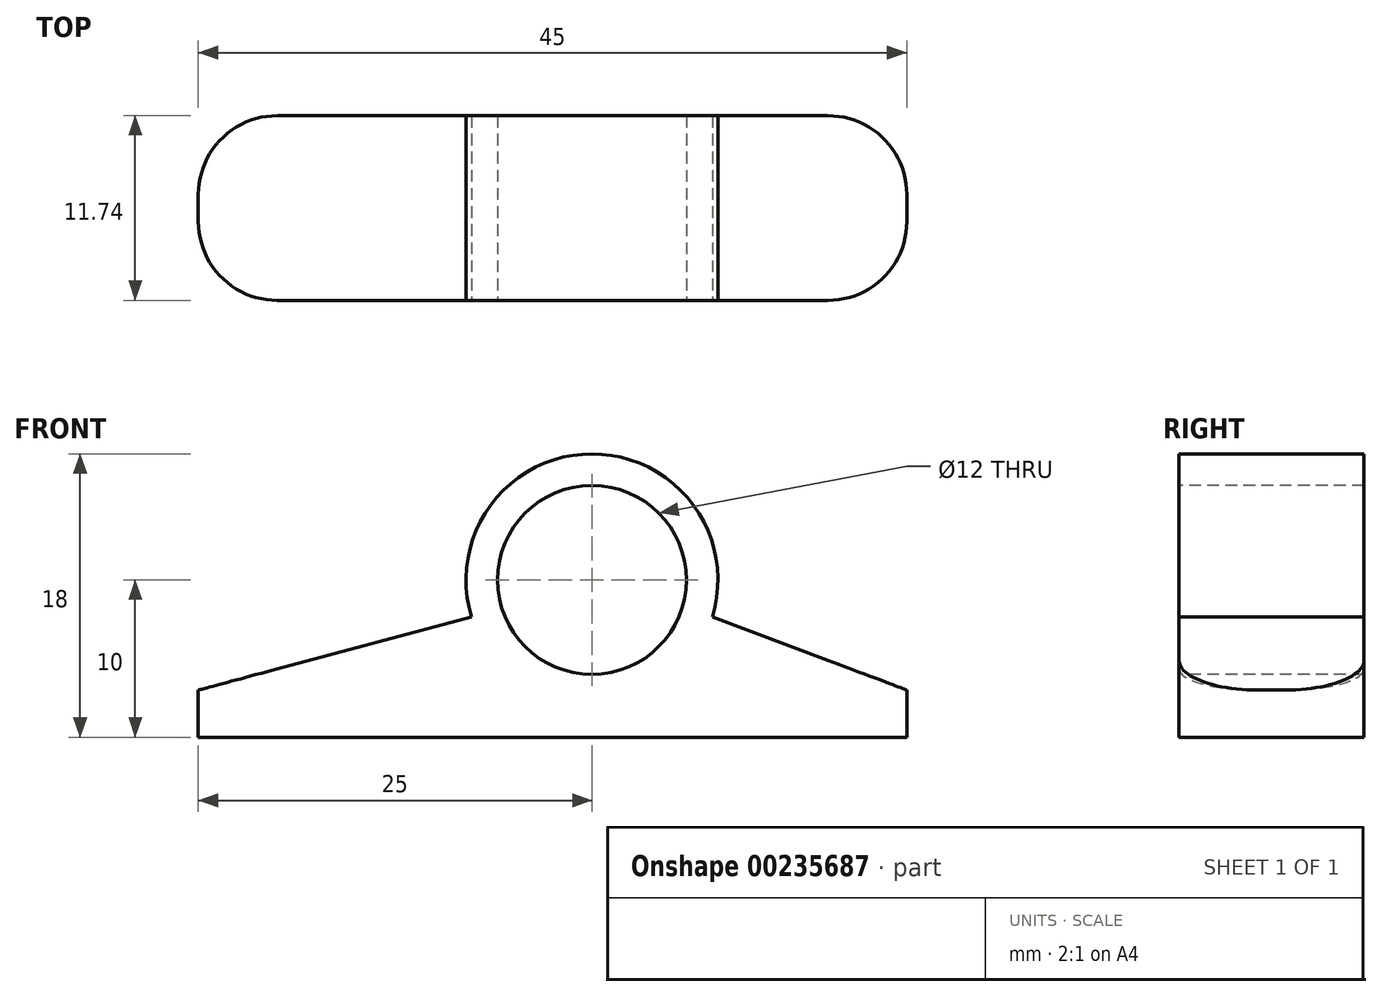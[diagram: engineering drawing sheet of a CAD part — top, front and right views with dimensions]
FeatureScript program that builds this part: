
annotation { "Feature Type Name" : "Feature", "Feature Type Description" : "" }
export const myFeature = defineFeature(function(context is Context, id is Id, definition is map)
    precondition{}
    {
        {
            var Q0;
            Q0=qCreatedBy(makeId("Top.planeOp"),FACE);
            var sketch = newSketch(context, id + "F0", { "sketchPlane" : qUnion([Q0])});
            skLineSegment(sketch, "E0.bottom", {"start": v(0, 0) * mm, "end": v(-45, 0) * mm});
            skLineSegment(sketch, "E0.left", {"start": v(0, 0) * mm, "end": v(0, 11.74) * mm});
            skLineSegment(sketch, "E0.right", {"start": v(-45, 0) * mm, "end": v(-45, 11.74) * mm});
            skLineSegment(sketch, "E1", {"start": v(0, 11.74) * mm, "end": v(-45, 11.74) * mm});
            skSolve(sketch);
        }
        {
            var Q0;
            Q0=makeQuery(id+"F0.imprint","IMPRINT",FACE,{"disambiguationData":[TD([[makeQuery(id+"F0.imprint","IMPRINT",EDGE,{"derivedFrom":sQuery(id+"F0.wireOp",EDGE,"E0.bottom")}),-1.0]])]});
            extrude(context, id + "F1", {"entities" : qUnion([Q0]), "depth" : 3 * mm});
        }
        {
            var Q0;
            Q0=qCreatedBy(makeId("Front.planeOp"),FACE);
            var sketch = newSketch(context, id + "F2", { "sketchPlane" : qUnion([Q0])});
            skCircle(sketch, "E2", {"center": v(-20, 10) * mm, "radius": 6 * mm});
            skLineSegment(sketch, "E3.0", {"start": v(0, 3) * mm, "end": v(-45, 3) * mm});
            skLineSegment(sketch, "E4", {"start": v(-20, 10) * mm, "end": v(-20, -23.23) * mm, "construction": true});
            skArc(sketch, "E5.trimOffspring", {"start": v(-12.35, 7.65) * mm, "mid": v(-20, 18) * mm, "end": v(-27.65, 7.65) * mm});
            skLineSegment(sketch, "E6", {"start": v(0, 0) * mm, "end": v(0, 3) * mm, "construction": true});
            skLineSegment(sketch, "E7.0", {"start": v(0, 0) * mm, "end": v(-45, 0) * mm, "construction": true});
            skLineSegment(sketch, "E8", {"start": v(-45, 0) * mm, "end": v(-45, 3) * mm, "construction": true});
            skLineSegment(sketch, "E9", {"start": v(-45, 3) * mm, "end": v(-27.65, 7.65) * mm});
            skLineSegment(sketch, "E10", {"start": v(0, 3) * mm, "end": v(-12.35, 7.65) * mm});
            skSolve(sketch);
        }
        {
            var Q0;
            Q0 = qSketchRegion(id + "F2", true);
            extrude(context, id + "F3", {"entities" : qUnion([Q0]), "operationType" : NewBodyOperationType.ADD, "oppositeDirection" : true, "depth" : 11.74 * mm});
        }
        {
            var Q0;
            Q0=makeQuery(id+"F1.opExtrude","SWEPT_EDGE",EDGE,{"disambiguationData":[OSD([sQuery(id+"F0.wireOp",EDGE,"E0.bottom"),sQuery(id+"F0.wireOp",EDGE,"E0.right")])]});
            var Q1;
            Q1=makeQuery(id+"F1.opExtrude","SWEPT_EDGE",EDGE,{"disambiguationData":[OSD([sQuery(id+"F0.wireOp",EDGE,"E0.bottom"),sQuery(id+"F0.wireOp",EDGE,"E0.left")])]});
            var Q2;
            Q2=makeQuery(id+"F1.opExtrude","SWEPT_EDGE",EDGE,{"disambiguationData":[OSD([sQuery(id+"F0.wireOp",EDGE,"E0.left"),sQuery(id+"F0.wireOp",EDGE,"E1")])]});
            var Q3;
            Q3=makeQuery(id+"F1.opExtrude","SWEPT_EDGE",EDGE,{"disambiguationData":[OSD([sQuery(id+"F0.wireOp",EDGE,"E0.right"),sQuery(id+"F0.wireOp",EDGE,"E1")])]});
            fillet(context, id + "F4", {"entities" : qUnion([Q0, Q1, Q2, Q3]), "radius" : 5 * mm, "tangentPropagation" : true, "allowEdgeOverflow" : false});
        }
    });
